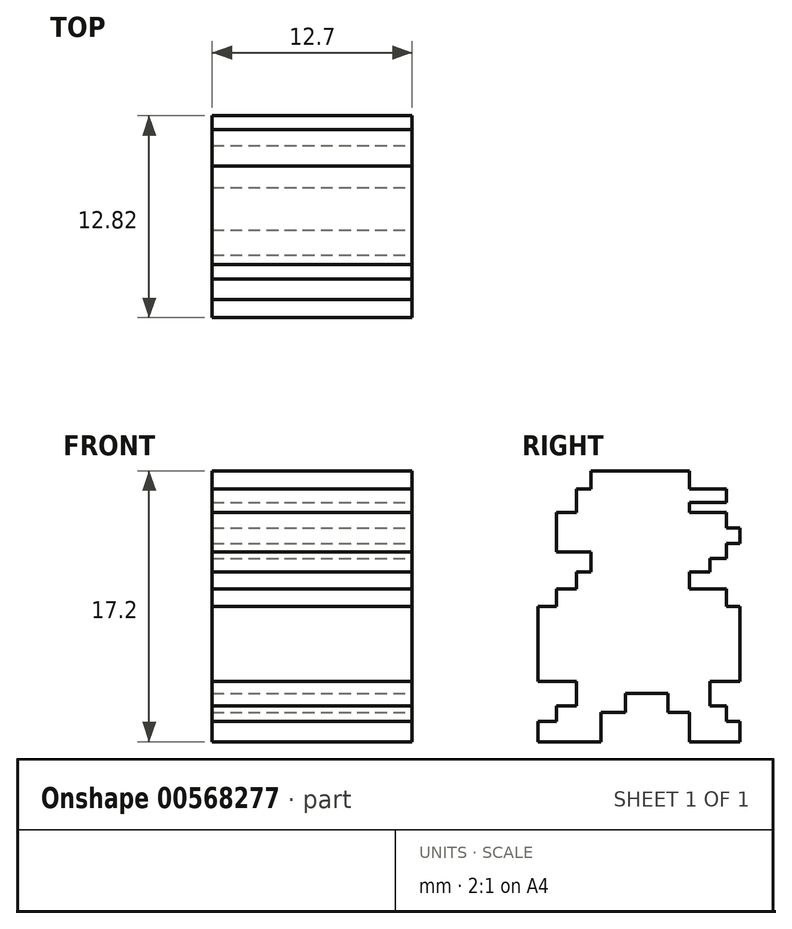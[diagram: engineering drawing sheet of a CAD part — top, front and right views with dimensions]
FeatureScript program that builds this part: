
annotation { "Feature Type Name" : "Feature", "Feature Type Description" : "" }
export const myFeature = defineFeature(function(context is Context, id is Id, definition is map)
    precondition{}
    {
        {
            var Q0;
            Q0=qCreatedBy(makeId("Right.planeOp"),FACE);
            var sketch = newSketch(context, id + "F0", { "sketchPlane" : qUnion([Q0])});
            skLineSegment(sketch, "E0", {"start": v(0, 0) * mm, "end": v(0, 25.4) * mm});
            skLineSegment(sketch, "E1", {"start": v(0, 25.4) * mm, "end": v(25.4, 25.4) * mm});
            skLineSegment(sketch, "E2", {"start": v(25.4, 25.4) * mm, "end": v(25.4, 0) * mm});
            skLineSegment(sketch, "E3", {"start": v(0, 0) * mm, "end": v(25.4, 0) * mm});
            skSolve(sketch);
        }
        {
            var Q0;
            Q0 = qSketchRegion(id + "F0", true);
            extrude(context, id + "F1", {"entities" : qUnion([Q0]), "depth" : 12.7 * mm, "offsetDistance" : 25.4 * mm});
        }
        {
            var Q0;
            Q0=makeQuery(id+"F1.opExtrude","CAP_FACE",FACE,{"disambiguationData":[OSD([sQuery(id+"F0.wireOp",EDGE,"E0"),sQuery(id+"F0.wireOp",EDGE,"E1"),sQuery(id+"F0.wireOp",EDGE,"E2"),sQuery(id+"F0.wireOp",EDGE,"E3")])],"isStart":false});
            var sketch = newSketch(context, id + "F2", { "sketchPlane" : qUnion([Q0])});
            skLineSegment(sketch, "E4", {"start": v(16.82, 0) * mm, "end": v(16.82, 1.88) * mm});
            skLineSegment(sketch, "E5", {"start": v(16.82, 1.88) * mm, "end": v(15.45, 1.88) * mm});
            skLineSegment(sketch, "E6", {"start": v(15.45, 1.88) * mm, "end": v(15.45, 3.08) * mm});
            skLineSegment(sketch, "E7", {"start": v(15.45, 3.08) * mm, "end": v(12.75, 3.08) * mm});
            skLineSegment(sketch, "E8", {"start": v(12.75, 3.08) * mm, "end": v(12.75, 1.88) * mm});
            skLineSegment(sketch, "E9", {"start": v(12.75, 1.88) * mm, "end": v(11.17, 1.88) * mm});
            skLineSegment(sketch, "E10", {"start": v(11.17, 1.88) * mm, "end": v(11.17, 0) * mm});
            skLineSegment(sketch, "E11", {"start": v(11.17, 0) * mm, "end": v(7.19, 0) * mm});
            skLineSegment(sketch, "E12", {"start": v(7.19, 0) * mm, "end": v(7.19, 1.3) * mm});
            skLineSegment(sketch, "E13", {"start": v(7.19, 1.3) * mm, "end": v(8.35, 1.3) * mm});
            skLineSegment(sketch, "E14", {"start": v(8.35, 1.3) * mm, "end": v(8.35, 2.3) * mm});
            skLineSegment(sketch, "E15", {"start": v(8.35, 2.3) * mm, "end": v(9.63, 2.3) * mm});
            skLineSegment(sketch, "E16", {"start": v(9.63, 2.3) * mm, "end": v(9.63, 3.83) * mm});
            skLineSegment(sketch, "E17", {"start": v(9.63, 3.83) * mm, "end": v(7.19, 3.83) * mm});
            skLineSegment(sketch, "E18", {"start": v(7.19, 3.83) * mm, "end": v(7.19, 8.6) * mm});
            skLineSegment(sketch, "E19", {"start": v(7.19, 8.6) * mm, "end": v(8.35, 8.6) * mm});
            skLineSegment(sketch, "E20", {"start": v(8.35, 8.6) * mm, "end": v(8.35, 9.72) * mm});
            skLineSegment(sketch, "E21", {"start": v(8.35, 9.72) * mm, "end": v(9.63, 9.72) * mm});
            skLineSegment(sketch, "E22", {"start": v(9.63, 9.72) * mm, "end": v(9.63, 10.8) * mm});
            skLineSegment(sketch, "E23", {"start": v(9.63, 10.8) * mm, "end": v(10.55, 10.8) * mm});
            skLineSegment(sketch, "E24", {"start": v(10.55, 10.8) * mm, "end": v(10.55, 12.05) * mm});
            skLineSegment(sketch, "E25", {"start": v(10.55, 12.05) * mm, "end": v(8.35, 12.05) * mm});
            skLineSegment(sketch, "E26", {"start": v(8.35, 12.05) * mm, "end": v(8.35, 14.58) * mm});
            skLineSegment(sketch, "E27", {"start": v(8.35, 14.58) * mm, "end": v(9.63, 14.58) * mm});
            skLineSegment(sketch, "E28", {"start": v(9.63, 14.58) * mm, "end": v(9.63, 16.07) * mm});
            skLineSegment(sketch, "E29", {"start": v(9.63, 16.07) * mm, "end": v(10.55, 16.07) * mm});
            skLineSegment(sketch, "E30", {"start": v(10.55, 16.07) * mm, "end": v(10.55, 17.2) * mm});
            skLineSegment(sketch, "E31", {"start": v(10.55, 17.2) * mm, "end": v(16.82, 17.2) * mm});
            skLineSegment(sketch, "E32", {"start": v(16.82, 17.2) * mm, "end": v(16.82, 16.07) * mm});
            skLineSegment(sketch, "E33", {"start": v(16.82, 16.07) * mm, "end": v(19.14, 16.07) * mm});
            skLineSegment(sketch, "E34", {"start": v(19.14, 16.07) * mm, "end": v(19.14, 15.2) * mm});
            skLineSegment(sketch, "E35", {"start": v(19.14, 15.2) * mm, "end": v(16.82, 15.2) * mm});
            skLineSegment(sketch, "E36", {"start": v(16.82, 15.2) * mm, "end": v(16.82, 14.58) * mm});
            skLineSegment(sketch, "E37", {"start": v(16.82, 14.58) * mm, "end": v(19.14, 14.58) * mm});
            skLineSegment(sketch, "E38", {"start": v(19.14, 14.58) * mm, "end": v(19.14, 13.58) * mm});
            skLineSegment(sketch, "E39", {"start": v(19.14, 13.58) * mm, "end": v(20.01, 13.58) * mm});
            skLineSegment(sketch, "E40", {"start": v(20.01, 13.58) * mm, "end": v(20.01, 12.59) * mm});
            skLineSegment(sketch, "E41", {"start": v(20.01, 12.59) * mm, "end": v(19.14, 12.59) * mm});
            skLineSegment(sketch, "E42", {"start": v(19.14, 12.59) * mm, "end": v(19.14, 11.63) * mm});
            skLineSegment(sketch, "E43", {"start": v(19.14, 11.63) * mm, "end": v(18.1, 11.63) * mm});
            skLineSegment(sketch, "E44", {"start": v(18.1, 11.63) * mm, "end": v(18.1, 10.8) * mm});
            skLineSegment(sketch, "E45", {"start": v(18.1, 10.8) * mm, "end": v(16.82, 10.8) * mm});
            skLineSegment(sketch, "E46", {"start": v(16.82, 10.8) * mm, "end": v(16.82, 9.72) * mm});
            skLineSegment(sketch, "E47", {"start": v(16.82, 9.72) * mm, "end": v(19.14, 9.72) * mm});
            skLineSegment(sketch, "E48", {"start": v(19.14, 9.72) * mm, "end": v(19.14, 8.6) * mm});
            skLineSegment(sketch, "E49", {"start": v(19.14, 8.6) * mm, "end": v(20.01, 8.6) * mm});
            skLineSegment(sketch, "E50", {"start": v(20.01, 8.6) * mm, "end": v(20.01, 3.83) * mm});
            skLineSegment(sketch, "E51", {"start": v(20.01, 3.83) * mm, "end": v(18.1, 3.83) * mm});
            skLineSegment(sketch, "E52", {"start": v(18.1, 3.83) * mm, "end": v(18.1, 2.3) * mm});
            skLineSegment(sketch, "E53", {"start": v(18.1, 2.3) * mm, "end": v(19.14, 2.3) * mm});
            skLineSegment(sketch, "E54", {"start": v(19.14, 2.3) * mm, "end": v(19.14, 1.3) * mm});
            skLineSegment(sketch, "E55", {"start": v(19.14, 1.3) * mm, "end": v(20.01, 1.3) * mm});
            skLineSegment(sketch, "E56", {"start": v(20.01, 1.3) * mm, "end": v(20.01, 0) * mm});
            skLineSegment(sketch, "E57", {"start": v(20.01, 0) * mm, "end": v(16.82, 0) * mm});
            skLineSegment(sketch, "E58", {"start": v(16.82, 15.2) * mm, "end": v(9.63, 15.2) * mm});
            skSolve(sketch);
        }
        {
            var Q0;
            {var subQ1=sQuery(id+"F2.wireOp",EDGE,"E12");Q0=makeQuery(id+"F2.imprint","IMPRINT",FACE,{"disambiguationData":[TD([[makeQuery(id+"F2.imprint","IMPRINT",EDGE,{"derivedFrom":subQ1}),1.0]])]});}
            var Q1;
            {var subQ0=sQuery(id+"F2.wireOp",EDGE,"E4");Q1=makeQuery(id+"F2.imprint","IMPRINT",FACE,{"disambiguationData":[TD([[makeQuery(id+"F2.imprint","IMPRINT",EDGE,{"derivedFrom":subQ0}),1.0]])]});}
            extrude(context, id + "F3", {"entities" : qUnion([Q0, Q1]), "operationType" : NewBodyOperationType.REMOVE, "oppositeDirection" : true, "depth" : 25.4 * mm, "offsetDistance" : 25.4 * mm});
        }
    });
